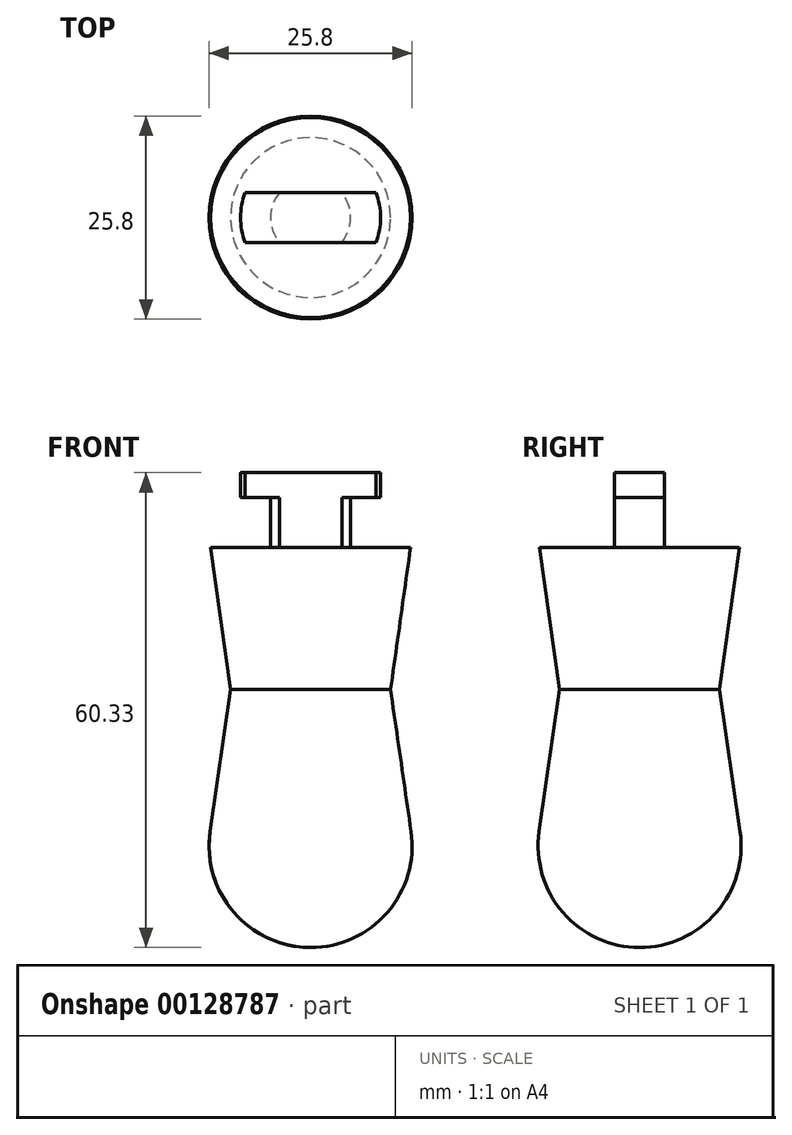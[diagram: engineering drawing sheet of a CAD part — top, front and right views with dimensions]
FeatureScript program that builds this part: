
annotation { "Feature Type Name" : "Feature", "Feature Type Description" : "" }
export const myFeature = defineFeature(function(context is Context, id is Id, definition is map)
    precondition{}
    {
        {
            var Q0;
            Q0=qCreatedBy(makeId("Front.planeOp"),FACE);
            var sketch = newSketch(context, id + "F0", { "sketchPlane" : qUnion([Q0])});
            skLineSegment(sketch, "E0", {"start": v(0, 0) * mm, "end": v(0, -50.8) * mm});
            skLineSegment(sketch, "E1", {"start": v(0, 0) * mm, "end": v(-12.7, 0) * mm});
            skLineSegment(sketch, "E2", {"start": v(0, -36.06) * mm, "end": v(-12.76, -36.06) * mm});
            skArc(sketch, "E3", {"start": v(-12.76, -36.06) * mm, "mid": v(-9.75, -46.35) * mm, "end": v(0, -50.8) * mm});
            skLineSegment(sketch, "E4", {"start": v(0, -18.03) * mm, "end": v(-10.16, -18.03) * mm});
            skLineSegment(sketch, "E5", {"start": v(-10.16, -18.03) * mm, "end": v(-12.7, 0) * mm});
            skLineSegment(sketch, "E6", {"start": v(-12.76, -36.06) * mm, "end": v(-10.16, -18.03) * mm});
            skLineSegment(sketch, "E7", {"start": v(0, 0) * mm, "end": v(-5.08, 0) * mm});
            skLineSegment(sketch, "E8", {"start": v(-5.08, 0) * mm, "end": v(-5.08, 6.35) * mm});
            skLineSegment(sketch, "E9", {"start": v(-5.08, 6.35) * mm, "end": v(-8.9, 6.35) * mm});
            skLineSegment(sketch, "E10", {"start": v(-8.9, 6.35) * mm, "end": v(-8.9, 9.53) * mm});
            skLineSegment(sketch, "E11", {"start": v(-8.9, 9.53) * mm, "end": v(0, 9.53) * mm});
            skLineSegment(sketch, "E12", {"start": v(0, 9.53) * mm, "end": v(0, 0) * mm});
            skPoint(sketch, "E13", {"position": v(0, -18.03) * mm});
            skLineSegment(sketch, "E14", {"start": v(0, -50.8) * mm, "end": v(16.53, -50.8) * mm, "construction": true});
            skLineSegment(sketch, "E15", {"start": v(0, 0) * mm, "end": v(0, -36.06) * mm});
            skSolve(sketch);
        }
        {
            var Q0;
            Q0=qSketchRegion(id+"F0",true);
            var Q1;
            Q1=sQuery(id+"F0.wireOp",EDGE,"E0");
            revolve(context, id + "F1", {"entities" : qUnion([Q0]), "axis" : qUnion([Q1]), "revolveType" : RevolveType.FULL});
        }
        {
            var Q0;
            Q0=makeQuery(id+"F1.opRevolve","SWEPT_FACE",FACE,{"disambiguationData":[OSD([sQuery(id+"F0.wireOp",EDGE,"E11")])]});
            var sketch = newSketch(context, id + "F2", { "sketchPlane" : qUnion([Q0])});
            skLineSegment(sketch, "E16.bottom", {"start": v(-18.75, 3.18) * mm, "end": v(18.75, 3.18) * mm});
            skLineSegment(sketch, "E16.top", {"start": v(-18.75, -3.18) * mm, "end": v(18.75, -3.18) * mm});
            skLineSegment(sketch, "E16.left", {"start": v(-18.75, 3.18) * mm, "end": v(-18.75, -3.18) * mm});
            skLineSegment(sketch, "E16.right", {"start": v(18.75, 3.18) * mm, "end": v(18.75, -3.18) * mm});
            skPoint(sketch, "E16.middle", {"position": v(0, 0) * mm});
            skCircle(sketch, "E17", {"center": v(0, 0) * mm, "radius": 11.42 * mm});
            skSolve(sketch);
        }
        {
            var Q0;
            {var subQ0=sQuery(id+"F2.wireOp",EDGE,"E16.bottom");var subQ1=makeQuery(id+"F1.opRevolve","SWEPT_EDGE",EDGE,{"disambiguationData":[OSD([sQuery(id+"F0.wireOp",EDGE,"E10"),sQuery(id+"F0.wireOp",EDGE,"E11")])]});var subQ2=makeQuery(id+"F2.imprint","INTERSECT",VERTEX,{"disambiguationData":[OD(0.0)],"derivedFrom":[subQ1,subQ0]});Q0=makeQuery(id+"F2.imprint","IMPRINT",FACE,{"disambiguationData":[TD([[makeQuery(id+"F2.imprint","IMPRINT",EDGE,{"disambiguationData":[TD([[subQ2,-1.0]])],"derivedFrom":subQ0}),1.0]])]});}
            var Q1;
            {var subQ0=sQuery(id+"F2.wireOp",EDGE,"E16.top");var subQ1=makeQuery(id+"F1.opRevolve","SWEPT_EDGE",EDGE,{"disambiguationData":[OSD([sQuery(id+"F0.wireOp",EDGE,"E10"),sQuery(id+"F0.wireOp",EDGE,"E11")])]});var subQ2=makeQuery(id+"F2.imprint","INTERSECT",VERTEX,{"disambiguationData":[OD(0.0)],"derivedFrom":[subQ1,subQ0]});Q1=makeQuery(id+"F2.imprint","IMPRINT",FACE,{"disambiguationData":[TD([[makeQuery(id+"F2.imprint","IMPRINT",EDGE,{"disambiguationData":[TD([[subQ2,-1.0]])],"derivedFrom":subQ0}),-1.0]])]});}
            var Q2;
            {var subQ0=sQuery(id+"F2.wireOp",EDGE,"E17");var subQ1=sQuery(id+"F2.wireOp",EDGE,"E16.bottom");var subQ2=makeQuery(id+"F2.imprint","INTERSECT",VERTEX,{"disambiguationData":[OD(0.0)],"derivedFrom":[subQ1,subQ0]});Q2=makeQuery(id+"F2.imprint","IMPRINT",FACE,{"disambiguationData":[TD([[makeQuery(id+"F2.imprint","IMPRINT",EDGE,{"disambiguationData":[TD([[subQ2,1.0]])],"derivedFrom":subQ0}),1.0]])]});}
            var Q3;
            {var subQ0=sQuery(id+"F2.wireOp",EDGE,"E17");var subQ1=sQuery(id+"F2.wireOp",EDGE,"E16.top");var subQ2=makeQuery(id+"F2.imprint","INTERSECT",VERTEX,{"disambiguationData":[OD(0.0)],"derivedFrom":[subQ1,subQ0]});Q3=makeQuery(id+"F2.imprint","IMPRINT",FACE,{"disambiguationData":[TD([[makeQuery(id+"F2.imprint","IMPRINT",EDGE,{"disambiguationData":[TD([[subQ2,-1.0]])],"derivedFrom":subQ0}),1.0]])]});}
            var Q4;
            {var subQ0=sQuery(id+"F2.wireOp",EDGE,"E17");var subQ1=sQuery(id+"F2.wireOp",EDGE,"E16.bottom");var subQ2=makeQuery(id+"F2.imprint","INTERSECT",VERTEX,{"disambiguationData":[OD(0.0)],"derivedFrom":[subQ1,subQ0]});Q4=makeQuery(id+"F2.imprint","IMPRINT",FACE,{"disambiguationData":[TD([[makeQuery(id+"F2.imprint","IMPRINT",EDGE,{"disambiguationData":[TD([[subQ2,-1.0]])],"derivedFrom":subQ0}),1.0]])]});}
            var Q5;
            {var subQ0=sQuery(id+"F2.wireOp",EDGE,"E17");var subQ1=sQuery(id+"F2.wireOp",EDGE,"E16.bottom");var subQ2=makeQuery(id+"F2.imprint","INTERSECT",VERTEX,{"disambiguationData":[OD(1.0)],"derivedFrom":[subQ1,subQ0]});Q5=makeQuery(id+"F2.imprint","IMPRINT",FACE,{"disambiguationData":[TD([[makeQuery(id+"F2.imprint","IMPRINT",EDGE,{"disambiguationData":[TD([[subQ2,1.0]])],"derivedFrom":subQ0}),1.0]])]});}
            var Q6;
            Q6=makeQuery(id+"F1.opRevolve","SWEPT_FACE",FACE,{"disambiguationData":[OSD([sQuery(id+"F0.wireOp",EDGE,"E1")])]});
            extrude(context, id + "F3", {"entities" : qUnion([Q0, Q1, Q2, Q3, Q4, Q5]), "operationType" : NewBodyOperationType.REMOVE, "endBound" : BoundingType.UP_TO_SURFACE, "oppositeDirection" : true, "endBoundEntityFace" : qUnion([Q6]), "depth" : 25.4 * mm});
        }
    });
